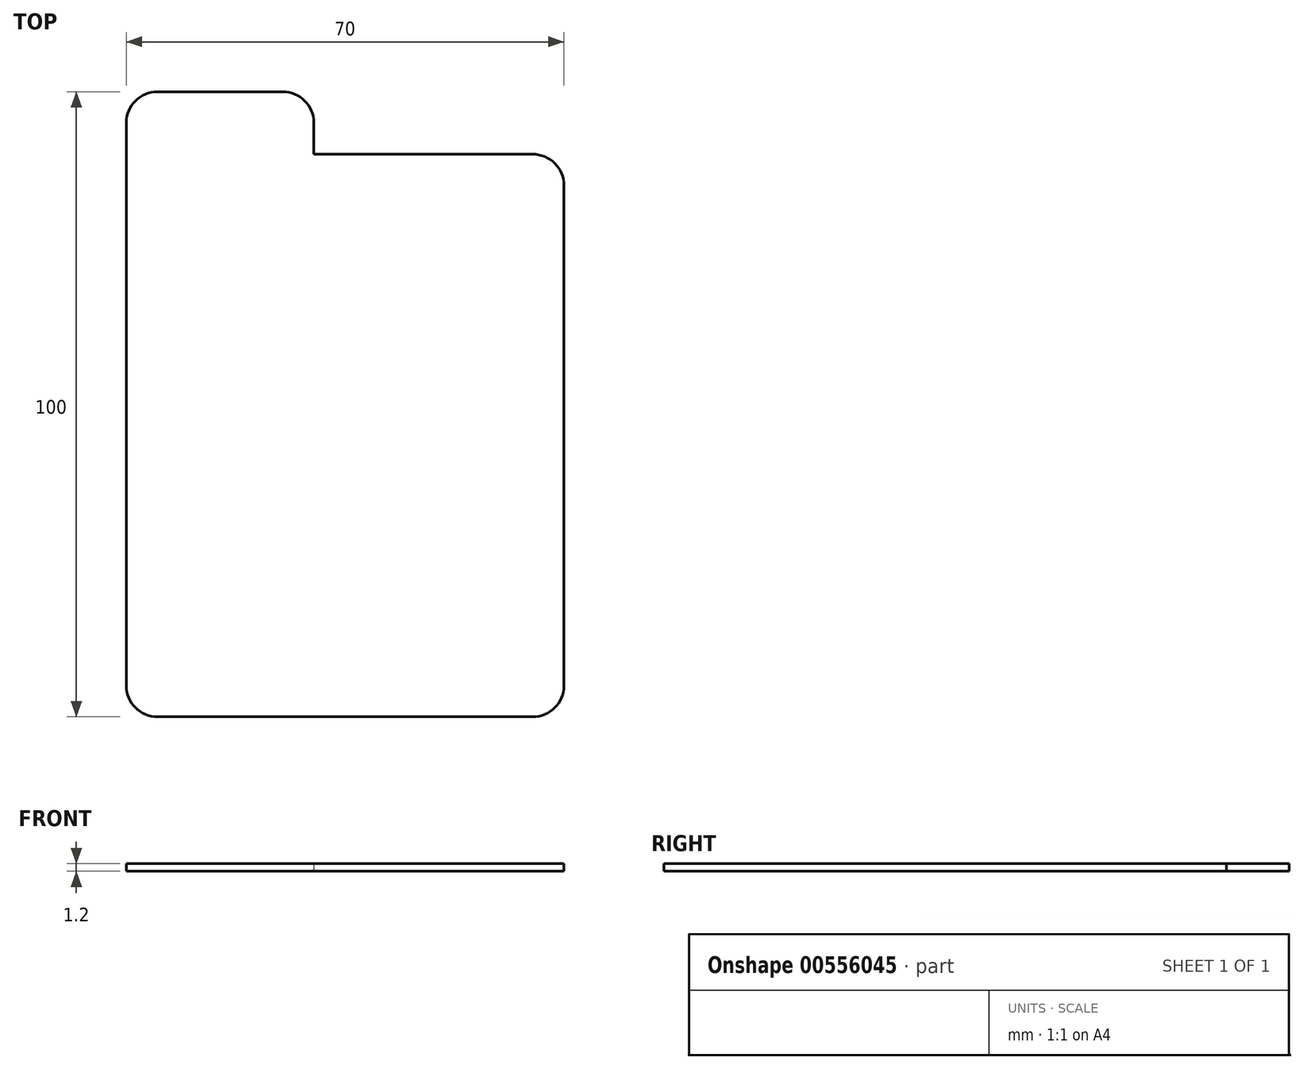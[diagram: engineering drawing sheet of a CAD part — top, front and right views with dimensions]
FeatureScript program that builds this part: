
annotation { "Feature Type Name" : "Feature", "Feature Type Description" : "" }
export const myFeature = defineFeature(function(context is Context, id is Id, definition is map)
    precondition{}
    {
        {
            var Q0;
            Q0=qCreatedBy(makeId("Top.planeOp"),FACE);
            var sketch = newSketch(context, id + "F0", { "sketchPlane" : qUnion([Q0])});
            skLineSegment(sketch, "E0.bottom", {"start": v(30, -50) * mm, "end": v(-30, -50) * mm});
            skLineSegment(sketch, "E0.left", {"start": v(35, -45) * mm, "end": v(35, 35) * mm});
            skLineSegment(sketch, "E0.right", {"start": v(-35, -45) * mm, "end": v(-35, 45) * mm});
            skPoint(sketch, "E0.middle", {"position": v(0, 0) * mm});
            skLineSegment(sketch, "E1", {"start": v(-30, 50) * mm, "end": v(-10, 50) * mm});
            skLineSegment(sketch, "E2", {"start": v(-5, 40) * mm, "end": v(30, 40) * mm});
            skLineSegment(sketch, "E3", {"start": v(-5, 45) * mm, "end": v(-5, 40) * mm});
            skPoint(sketch, "E4.visualSharp", {"position": v(-5, 50) * mm});
            skArc(sketch, "E4.filletArc", {"start": v(-5, 45) * mm, "mid": v(-6.46, 48.54) * mm, "end": v(-10, 50) * mm});
            skPoint(sketch, "E5.visualSharp", {"position": v(-35, 50) * mm});
            skArc(sketch, "E5.filletArc", {"start": v(-30, 50) * mm, "mid": v(-33.54, 48.54) * mm, "end": v(-35, 45) * mm});
            skPoint(sketch, "E6.visualSharp", {"position": v(35, 40) * mm});
            skArc(sketch, "E6.filletArc", {"start": v(35, 35) * mm, "mid": v(33.54, 38.54) * mm, "end": v(30, 40) * mm});
            skPoint(sketch, "E7.visualSharp", {"position": v(35, -50) * mm});
            skArc(sketch, "E7.filletArc", {"start": v(30, -50) * mm, "mid": v(33.54, -48.54) * mm, "end": v(35, -45) * mm});
            skPoint(sketch, "E8.visualSharp", {"position": v(-35, -50) * mm});
            skArc(sketch, "E8.filletArc", {"start": v(-35, -45) * mm, "mid": v(-33.54, -48.54) * mm, "end": v(-30, -50) * mm});
            skSolve(sketch);
        }
        {
            var Q0;
            Q0 = qSketchRegion(id + "F0", true);
            extrude(context, id + "F1", {"entities" : qUnion([Q0]), "depth" : 1.2 * mm, "offsetDistance" : 25 * mm});
        }
    });
